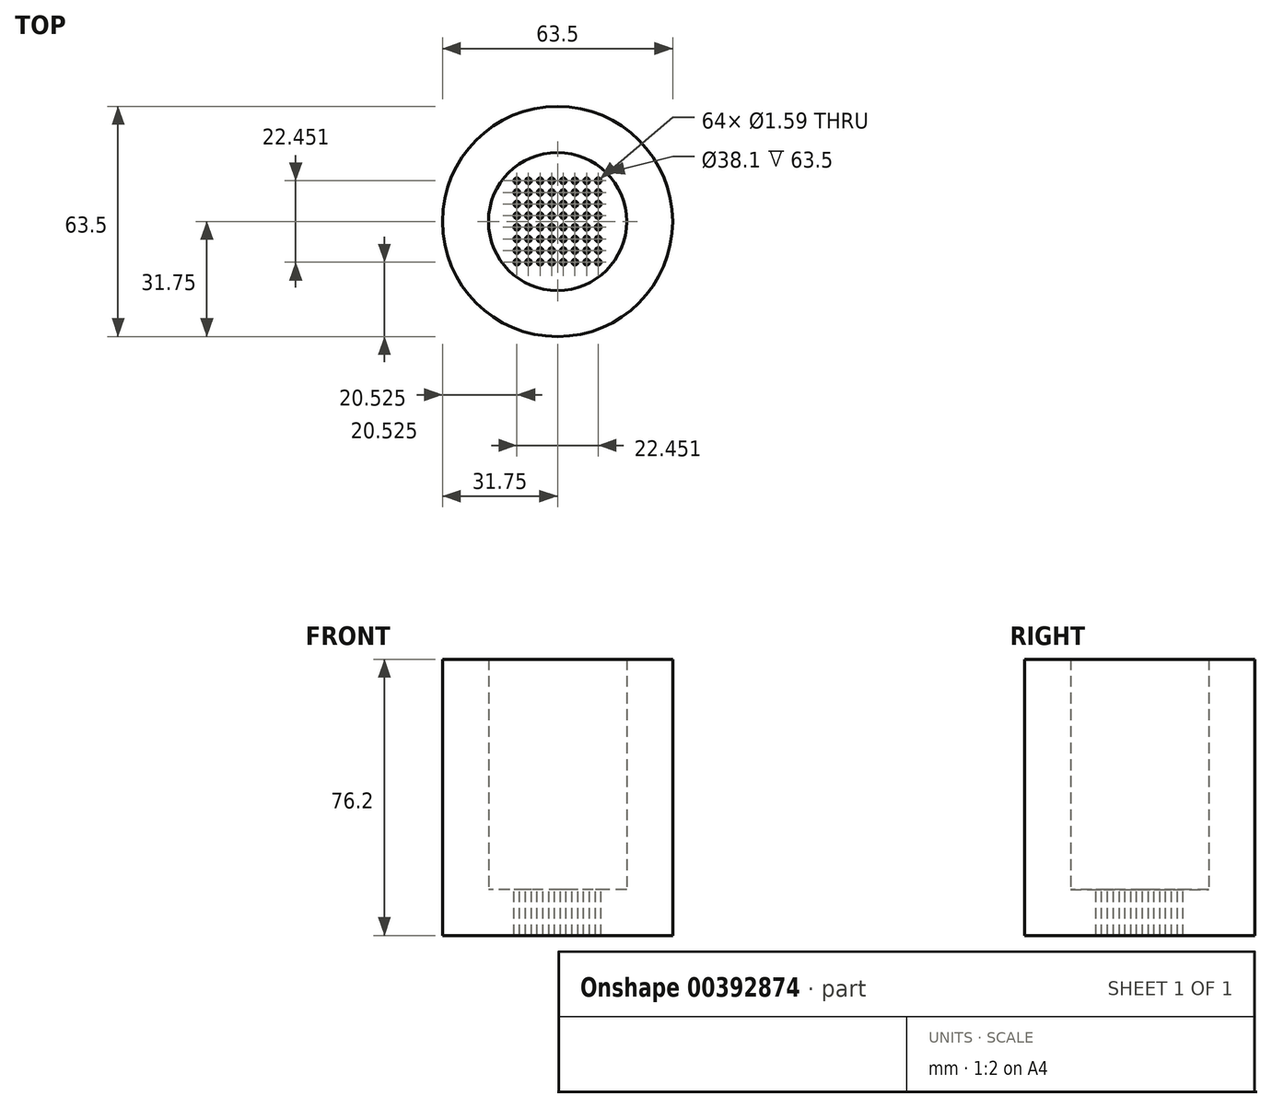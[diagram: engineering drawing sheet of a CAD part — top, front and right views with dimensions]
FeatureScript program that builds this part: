
annotation { "Feature Type Name" : "Feature", "Feature Type Description" : "" }
export const myFeature = defineFeature(function(context is Context, id is Id, definition is map)
    precondition{}
    {
        {
            var Q0;
            Q0=qCreatedBy(makeId("Top.planeOp"),FACE);
            var sketch = newSketch(context, id + "F0", { "sketchPlane" : qUnion([Q0])});
            skCircle(sketch, "E0", {"center": v(0, 0) * mm, "radius": 31.75 * mm});
            skSolve(sketch);
        }
        {
            var Q0;
            Q0=makeQuery(id+"F0.imprint","IMPRINT",FACE,{"disambiguationData":[TD([[makeQuery(id+"F0.imprint","IMPRINT",EDGE,{"derivedFrom":sQuery(id+"F0.wireOp",EDGE,"E0")}),1.0]])]});
            extrude(context, id + "F1", {"entities" : qUnion([Q0]), "depth" : 76.2 * mm});
        }
        {
            var Q0;
            Q0=makeQuery(id+"F1.opExtrude","CAP_FACE",FACE,{"disambiguationData":[OSD([sQuery(id+"F0.wireOp",EDGE,"E0")])],"isStart":false});
            shell(context, id + "F2", {"entities" : qUnion([Q0]), "thickness" : 12.7 * mm});
        }
        {
            var Q0;
            {var subQ0=sQuery(id+"F0.wireOp",EDGE,"E0");Q0=makeQuery(id+"F2.opShell","OFFSET_FACE",FACE,{"disambiguationData":[OSD([subQ0]),TDD([makeQuery(id+"F1.opExtrude","CAP_FACE",FACE,{"disambiguationData":[OSD([subQ0])],"isStart":true})])]});}
            var sketch = newSketch(context, id + "F3", { "sketchPlane" : qUnion([Q0])});
            skCircle(sketch, "E1.0", {"center": v(0, 0) * mm, "radius": 15.87 * mm, "construction": true});
            skLineSegment(sketch, "E2.bottom", {"start": v(-11.23, 11.23) * mm, "end": v(11.23, 11.23) * mm, "construction": true});
            skLineSegment(sketch, "E2.top", {"start": v(-11.23, -11.23) * mm, "end": v(11.23, -11.23) * mm, "construction": true});
            skLineSegment(sketch, "E2.left", {"start": v(-11.23, 11.23) * mm, "end": v(-11.23, -11.23) * mm, "construction": true});
            skLineSegment(sketch, "E2.right", {"start": v(11.23, 11.23) * mm, "end": v(11.23, -11.23) * mm, "construction": true});
            skCircle(sketch, "E3", {"center": v(-11.23, -11.23) * mm, "radius": 0.8 * mm});
            skCircle(sketch, "E4.1.0.0", {"center": v(-8.02, -11.23) * mm, "radius": 0.8 * mm});
            skCircle(sketch, "E4.2.0.0", {"center": v(-4.81, -11.23) * mm, "radius": 0.8 * mm});
            skCircle(sketch, "E4.3.0.0", {"center": v(-1.6, -11.23) * mm, "radius": 0.8 * mm});
            skCircle(sketch, "E4.4.0.0", {"center": v(1.6, -11.23) * mm, "radius": 0.8 * mm});
            skCircle(sketch, "E4.5.0.0", {"center": v(4.81, -11.23) * mm, "radius": 0.8 * mm});
            skCircle(sketch, "E4.6.0.0", {"center": v(8.02, -11.23) * mm, "radius": 0.8 * mm});
            skCircle(sketch, "E4.7.0.0", {"center": v(11.23, -11.23) * mm, "radius": 0.8 * mm});
            skLineSegment(sketch, "E4.direction1", {"start": v(-11.23, -11.23) * mm, "end": v(-8.02, -11.23) * mm, "construction": true});
            skCircle(sketch, "E5.1.0.0", {"center": v(-11.23, -8.02) * mm, "radius": 0.8 * mm});
            skCircle(sketch, "E5.1.0.1", {"center": v(-8.02, -8.02) * mm, "radius": 0.8 * mm});
            skCircle(sketch, "E5.1.0.2", {"center": v(-4.81, -8.02) * mm, "radius": 0.8 * mm});
            skCircle(sketch, "E5.1.0.3", {"center": v(-1.6, -8.02) * mm, "radius": 0.8 * mm});
            skCircle(sketch, "E5.1.0.4", {"center": v(1.6, -8.02) * mm, "radius": 0.8 * mm});
            skCircle(sketch, "E5.1.0.5", {"center": v(4.81, -8.02) * mm, "radius": 0.8 * mm});
            skCircle(sketch, "E5.1.0.6", {"center": v(8.02, -8.02) * mm, "radius": 0.8 * mm});
            skCircle(sketch, "E5.1.0.7", {"center": v(11.23, -8.02) * mm, "radius": 0.8 * mm});
            skCircle(sketch, "E5.2.0.0", {"center": v(-11.23, -4.81) * mm, "radius": 0.8 * mm});
            skCircle(sketch, "E5.2.0.1", {"center": v(-8.02, -4.81) * mm, "radius": 0.8 * mm});
            skCircle(sketch, "E5.2.0.2", {"center": v(-4.81, -4.81) * mm, "radius": 0.8 * mm});
            skCircle(sketch, "E5.2.0.3", {"center": v(-1.6, -4.81) * mm, "radius": 0.8 * mm});
            skCircle(sketch, "E5.2.0.4", {"center": v(1.6, -4.81) * mm, "radius": 0.8 * mm});
            skCircle(sketch, "E5.2.0.5", {"center": v(4.81, -4.81) * mm, "radius": 0.8 * mm});
            skCircle(sketch, "E5.2.0.6", {"center": v(8.02, -4.81) * mm, "radius": 0.8 * mm});
            skCircle(sketch, "E5.2.0.7", {"center": v(11.23, -4.81) * mm, "radius": 0.8 * mm});
            skCircle(sketch, "E5.3.0.0", {"center": v(-11.23, -1.6) * mm, "radius": 0.8 * mm});
            skCircle(sketch, "E5.3.0.1", {"center": v(-8.02, -1.6) * mm, "radius": 0.8 * mm});
            skCircle(sketch, "E5.3.0.2", {"center": v(-4.81, -1.6) * mm, "radius": 0.8 * mm});
            skCircle(sketch, "E5.3.0.3", {"center": v(-1.6, -1.6) * mm, "radius": 0.8 * mm});
            skCircle(sketch, "E5.3.0.4", {"center": v(1.6, -1.6) * mm, "radius": 0.8 * mm});
            skCircle(sketch, "E5.3.0.5", {"center": v(4.81, -1.6) * mm, "radius": 0.8 * mm});
            skCircle(sketch, "E5.3.0.6", {"center": v(8.02, -1.6) * mm, "radius": 0.8 * mm});
            skCircle(sketch, "E5.3.0.7", {"center": v(11.23, -1.6) * mm, "radius": 0.8 * mm});
            skCircle(sketch, "E5.4.0.0", {"center": v(-11.23, 1.6) * mm, "radius": 0.8 * mm});
            skCircle(sketch, "E5.4.0.1", {"center": v(-8.02, 1.6) * mm, "radius": 0.8 * mm});
            skCircle(sketch, "E5.4.0.2", {"center": v(-4.81, 1.6) * mm, "radius": 0.8 * mm});
            skCircle(sketch, "E5.4.0.3", {"center": v(-1.6, 1.6) * mm, "radius": 0.8 * mm});
            skCircle(sketch, "E5.4.0.4", {"center": v(1.6, 1.6) * mm, "radius": 0.8 * mm});
            skCircle(sketch, "E5.4.0.5", {"center": v(4.81, 1.6) * mm, "radius": 0.8 * mm});
            skCircle(sketch, "E5.4.0.6", {"center": v(8.02, 1.6) * mm, "radius": 0.8 * mm});
            skCircle(sketch, "E5.4.0.7", {"center": v(11.23, 1.6) * mm, "radius": 0.8 * mm});
            skCircle(sketch, "E5.5.0.0", {"center": v(-11.23, 4.81) * mm, "radius": 0.8 * mm});
            skCircle(sketch, "E5.5.0.1", {"center": v(-8.02, 4.81) * mm, "radius": 0.8 * mm});
            skCircle(sketch, "E5.5.0.2", {"center": v(-4.81, 4.81) * mm, "radius": 0.8 * mm});
            skCircle(sketch, "E5.5.0.3", {"center": v(-1.6, 4.81) * mm, "radius": 0.8 * mm});
            skCircle(sketch, "E5.5.0.4", {"center": v(1.6, 4.81) * mm, "radius": 0.8 * mm});
            skCircle(sketch, "E5.5.0.5", {"center": v(4.81, 4.81) * mm, "radius": 0.8 * mm});
            skCircle(sketch, "E5.5.0.6", {"center": v(8.02, 4.81) * mm, "radius": 0.8 * mm});
            skCircle(sketch, "E5.5.0.7", {"center": v(11.23, 4.81) * mm, "radius": 0.8 * mm});
            skCircle(sketch, "E5.6.0.0", {"center": v(-11.23, 8.02) * mm, "radius": 0.8 * mm});
            skCircle(sketch, "E5.6.0.1", {"center": v(-8.02, 8.02) * mm, "radius": 0.8 * mm});
            skCircle(sketch, "E5.6.0.2", {"center": v(-4.81, 8.02) * mm, "radius": 0.8 * mm});
            skCircle(sketch, "E5.6.0.3", {"center": v(-1.6, 8.02) * mm, "radius": 0.8 * mm});
            skCircle(sketch, "E5.6.0.4", {"center": v(1.6, 8.02) * mm, "radius": 0.8 * mm});
            skCircle(sketch, "E5.6.0.5", {"center": v(4.81, 8.02) * mm, "radius": 0.8 * mm});
            skCircle(sketch, "E5.6.0.6", {"center": v(8.02, 8.02) * mm, "radius": 0.8 * mm});
            skCircle(sketch, "E5.6.0.7", {"center": v(11.23, 8.02) * mm, "radius": 0.8 * mm});
            skCircle(sketch, "E5.7.0.0", {"center": v(-11.23, 11.23) * mm, "radius": 0.8 * mm});
            skCircle(sketch, "E5.7.0.1", {"center": v(-8.02, 11.23) * mm, "radius": 0.8 * mm});
            skCircle(sketch, "E5.7.0.2", {"center": v(-4.81, 11.23) * mm, "radius": 0.8 * mm});
            skCircle(sketch, "E5.7.0.3", {"center": v(-1.6, 11.23) * mm, "radius": 0.8 * mm});
            skCircle(sketch, "E5.7.0.4", {"center": v(1.6, 11.23) * mm, "radius": 0.8 * mm});
            skCircle(sketch, "E5.7.0.5", {"center": v(4.81, 11.23) * mm, "radius": 0.8 * mm});
            skCircle(sketch, "E5.7.0.6", {"center": v(8.02, 11.23) * mm, "radius": 0.8 * mm});
            skCircle(sketch, "E5.7.0.7", {"center": v(11.23, 11.23) * mm, "radius": 0.8 * mm});
            skLineSegment(sketch, "E5.direction1", {"start": v(-11.23, -11.23) * mm, "end": v(-11.23, -8.02) * mm, "construction": true});
            skSolve(sketch);
        }
        {
            var Q0;
            Q0=makeQuery(id+"F3.imprint","IMPRINT",FACE,{"disambiguationData":[TD([[makeQuery(id+"F3.imprint","IMPRINT",EDGE,{"derivedFrom":sQuery(id+"F3.wireOp",EDGE,"E4.7.0.0")}),1.0]])]});
            var Q1;
            Q1=makeQuery(id+"F3.imprint","IMPRINT",FACE,{"disambiguationData":[TD([[makeQuery(id+"F3.imprint","IMPRINT",EDGE,{"derivedFrom":sQuery(id+"F3.wireOp",EDGE,"E5.1.0.7")}),1.0]])]});
            var Q2;
            Q2=makeQuery(id+"F3.imprint","IMPRINT",FACE,{"disambiguationData":[TD([[makeQuery(id+"F3.imprint","IMPRINT",EDGE,{"derivedFrom":sQuery(id+"F3.wireOp",EDGE,"E5.2.0.7")}),1.0]])]});
            var Q3;
            Q3=makeQuery(id+"F3.imprint","IMPRINT",FACE,{"disambiguationData":[TD([[makeQuery(id+"F3.imprint","IMPRINT",EDGE,{"derivedFrom":sQuery(id+"F3.wireOp",EDGE,"E5.3.0.7")}),1.0]])]});
            var Q4;
            Q4=makeQuery(id+"F3.imprint","IMPRINT",FACE,{"disambiguationData":[TD([[makeQuery(id+"F3.imprint","IMPRINT",EDGE,{"derivedFrom":sQuery(id+"F3.wireOp",EDGE,"E5.4.0.7")}),1.0]])]});
            var Q5;
            Q5=makeQuery(id+"F3.imprint","IMPRINT",FACE,{"disambiguationData":[TD([[makeQuery(id+"F3.imprint","IMPRINT",EDGE,{"derivedFrom":sQuery(id+"F3.wireOp",EDGE,"E5.5.0.7")}),1.0]])]});
            var Q6;
            Q6=makeQuery(id+"F3.imprint","IMPRINT",FACE,{"disambiguationData":[TD([[makeQuery(id+"F3.imprint","IMPRINT",EDGE,{"derivedFrom":sQuery(id+"F3.wireOp",EDGE,"E5.5.0.6")}),1.0]])]});
            var Q7;
            Q7=makeQuery(id+"F3.imprint","IMPRINT",FACE,{"disambiguationData":[TD([[makeQuery(id+"F3.imprint","IMPRINT",EDGE,{"derivedFrom":sQuery(id+"F3.wireOp",EDGE,"E5.6.0.7")}),1.0]])]});
            var Q8;
            Q8=makeQuery(id+"F3.imprint","IMPRINT",FACE,{"disambiguationData":[TD([[makeQuery(id+"F3.imprint","IMPRINT",EDGE,{"derivedFrom":sQuery(id+"F3.wireOp",EDGE,"E5.7.0.7")}),1.0]])]});
            var Q9;
            Q9=makeQuery(id+"F3.imprint","IMPRINT",FACE,{"disambiguationData":[TD([[makeQuery(id+"F3.imprint","IMPRINT",EDGE,{"derivedFrom":sQuery(id+"F3.wireOp",EDGE,"E5.7.0.6")}),1.0]])]});
            var Q10;
            Q10=makeQuery(id+"F3.imprint","IMPRINT",FACE,{"disambiguationData":[TD([[makeQuery(id+"F3.imprint","IMPRINT",EDGE,{"derivedFrom":sQuery(id+"F3.wireOp",EDGE,"E5.6.0.6")}),1.0]])]});
            var Q11;
            Q11=makeQuery(id+"F3.imprint","IMPRINT",FACE,{"disambiguationData":[TD([[makeQuery(id+"F3.imprint","IMPRINT",EDGE,{"derivedFrom":sQuery(id+"F3.wireOp",EDGE,"E5.4.0.6")}),1.0]])]});
            var Q12;
            Q12=makeQuery(id+"F3.imprint","IMPRINT",FACE,{"disambiguationData":[TD([[makeQuery(id+"F3.imprint","IMPRINT",EDGE,{"derivedFrom":sQuery(id+"F3.wireOp",EDGE,"E5.3.0.6")}),1.0]])]});
            var Q13;
            Q13=makeQuery(id+"F3.imprint","IMPRINT",FACE,{"disambiguationData":[TD([[makeQuery(id+"F3.imprint","IMPRINT",EDGE,{"derivedFrom":sQuery(id+"F3.wireOp",EDGE,"E5.2.0.6")}),1.0]])]});
            var Q14;
            Q14=makeQuery(id+"F3.imprint","IMPRINT",FACE,{"disambiguationData":[TD([[makeQuery(id+"F3.imprint","IMPRINT",EDGE,{"derivedFrom":sQuery(id+"F3.wireOp",EDGE,"E4.6.0.0")}),1.0]])]});
            var Q15;
            Q15=makeQuery(id+"F3.imprint","IMPRINT",FACE,{"disambiguationData":[TD([[makeQuery(id+"F3.imprint","IMPRINT",EDGE,{"derivedFrom":sQuery(id+"F3.wireOp",EDGE,"E5.1.0.6")}),1.0]])]});
            var Q16;
            Q16=makeQuery(id+"F3.imprint","IMPRINT",FACE,{"disambiguationData":[TD([[makeQuery(id+"F3.imprint","IMPRINT",EDGE,{"derivedFrom":sQuery(id+"F3.wireOp",EDGE,"E5.1.0.5")}),1.0]])]});
            var Q17;
            Q17=makeQuery(id+"F3.imprint","IMPRINT",FACE,{"disambiguationData":[TD([[makeQuery(id+"F3.imprint","IMPRINT",EDGE,{"derivedFrom":sQuery(id+"F3.wireOp",EDGE,"E4.5.0.0")}),1.0]])]});
            var Q18;
            Q18=makeQuery(id+"F3.imprint","IMPRINT",FACE,{"disambiguationData":[TD([[makeQuery(id+"F3.imprint","IMPRINT",EDGE,{"derivedFrom":sQuery(id+"F3.wireOp",EDGE,"E5.2.0.5")}),1.0]])]});
            var Q19;
            Q19=makeQuery(id+"F3.imprint","IMPRINT",FACE,{"disambiguationData":[TD([[makeQuery(id+"F3.imprint","IMPRINT",EDGE,{"derivedFrom":sQuery(id+"F3.wireOp",EDGE,"E5.3.0.5")}),1.0]])]});
            var Q20;
            Q20=makeQuery(id+"F3.imprint","IMPRINT",FACE,{"disambiguationData":[TD([[makeQuery(id+"F3.imprint","IMPRINT",EDGE,{"derivedFrom":sQuery(id+"F3.wireOp",EDGE,"E5.4.0.5")}),1.0]])]});
            var Q21;
            Q21=makeQuery(id+"F3.imprint","IMPRINT",FACE,{"disambiguationData":[TD([[makeQuery(id+"F3.imprint","IMPRINT",EDGE,{"derivedFrom":sQuery(id+"F3.wireOp",EDGE,"E5.5.0.5")}),1.0]])]});
            var Q22;
            Q22=makeQuery(id+"F3.imprint","IMPRINT",FACE,{"disambiguationData":[TD([[makeQuery(id+"F3.imprint","IMPRINT",EDGE,{"derivedFrom":sQuery(id+"F3.wireOp",EDGE,"E5.6.0.5")}),1.0]])]});
            var Q23;
            Q23=makeQuery(id+"F3.imprint","IMPRINT",FACE,{"disambiguationData":[TD([[makeQuery(id+"F3.imprint","IMPRINT",EDGE,{"derivedFrom":sQuery(id+"F3.wireOp",EDGE,"E5.7.0.5")}),1.0]])]});
            var Q24;
            Q24=makeQuery(id+"F3.imprint","IMPRINT",FACE,{"disambiguationData":[TD([[makeQuery(id+"F3.imprint","IMPRINT",EDGE,{"derivedFrom":sQuery(id+"F3.wireOp",EDGE,"E4.4.0.0")}),1.0]])]});
            var Q25;
            Q25=makeQuery(id+"F3.imprint","IMPRINT",FACE,{"disambiguationData":[TD([[makeQuery(id+"F3.imprint","IMPRINT",EDGE,{"derivedFrom":sQuery(id+"F3.wireOp",EDGE,"E5.2.0.4")}),1.0]])]});
            var Q26;
            Q26=makeQuery(id+"F3.imprint","IMPRINT",FACE,{"disambiguationData":[TD([[makeQuery(id+"F3.imprint","IMPRINT",EDGE,{"derivedFrom":sQuery(id+"F3.wireOp",EDGE,"E5.1.0.4")}),1.0]])]});
            var Q27;
            Q27=makeQuery(id+"F3.imprint","IMPRINT",FACE,{"disambiguationData":[TD([[makeQuery(id+"F3.imprint","IMPRINT",EDGE,{"derivedFrom":sQuery(id+"F3.wireOp",EDGE,"E5.3.0.4")}),1.0]])]});
            var Q28;
            Q28=makeQuery(id+"F3.imprint","IMPRINT",FACE,{"disambiguationData":[TD([[makeQuery(id+"F3.imprint","IMPRINT",EDGE,{"derivedFrom":sQuery(id+"F3.wireOp",EDGE,"E5.4.0.4")}),1.0]])]});
            var Q29;
            Q29=makeQuery(id+"F3.imprint","IMPRINT",FACE,{"disambiguationData":[TD([[makeQuery(id+"F3.imprint","IMPRINT",EDGE,{"derivedFrom":sQuery(id+"F3.wireOp",EDGE,"E5.5.0.4")}),1.0]])]});
            var Q30;
            Q30=makeQuery(id+"F3.imprint","IMPRINT",FACE,{"disambiguationData":[TD([[makeQuery(id+"F3.imprint","IMPRINT",EDGE,{"derivedFrom":sQuery(id+"F3.wireOp",EDGE,"E5.6.0.4")}),1.0]])]});
            var Q31;
            Q31=makeQuery(id+"F3.imprint","IMPRINT",FACE,{"disambiguationData":[TD([[makeQuery(id+"F3.imprint","IMPRINT",EDGE,{"derivedFrom":sQuery(id+"F3.wireOp",EDGE,"E5.7.0.4")}),1.0]])]});
            var Q32;
            Q32=makeQuery(id+"F3.imprint","IMPRINT",FACE,{"disambiguationData":[TD([[makeQuery(id+"F3.imprint","IMPRINT",EDGE,{"derivedFrom":sQuery(id+"F3.wireOp",EDGE,"E5.7.0.3")}),1.0]])]});
            var Q33;
            Q33=makeQuery(id+"F3.imprint","IMPRINT",FACE,{"disambiguationData":[TD([[makeQuery(id+"F3.imprint","IMPRINT",EDGE,{"derivedFrom":sQuery(id+"F3.wireOp",EDGE,"E4.3.0.0")}),1.0]])]});
            var Q34;
            Q34=makeQuery(id+"F3.imprint","IMPRINT",FACE,{"disambiguationData":[TD([[makeQuery(id+"F3.imprint","IMPRINT",EDGE,{"derivedFrom":sQuery(id+"F3.wireOp",EDGE,"E4.2.0.0")}),1.0]])]});
            var Q35;
            Q35=makeQuery(id+"F3.imprint","IMPRINT",FACE,{"disambiguationData":[TD([[makeQuery(id+"F3.imprint","IMPRINT",EDGE,{"derivedFrom":sQuery(id+"F3.wireOp",EDGE,"E5.1.0.2")}),1.0]])]});
            var Q36;
            Q36=makeQuery(id+"F3.imprint","IMPRINT",FACE,{"disambiguationData":[TD([[makeQuery(id+"F3.imprint","IMPRINT",EDGE,{"derivedFrom":sQuery(id+"F3.wireOp",EDGE,"E5.1.0.3")}),1.0]])]});
            var Q37;
            Q37=makeQuery(id+"F3.imprint","IMPRINT",FACE,{"disambiguationData":[TD([[makeQuery(id+"F3.imprint","IMPRINT",EDGE,{"derivedFrom":sQuery(id+"F3.wireOp",EDGE,"E5.2.0.3")}),1.0]])]});
            var Q38;
            Q38=makeQuery(id+"F3.imprint","IMPRINT",FACE,{"disambiguationData":[TD([[makeQuery(id+"F3.imprint","IMPRINT",EDGE,{"derivedFrom":sQuery(id+"F3.wireOp",EDGE,"E5.2.0.2")}),1.0]])]});
            var Q39;
            Q39=makeQuery(id+"F3.imprint","IMPRINT",FACE,{"disambiguationData":[TD([[makeQuery(id+"F3.imprint","IMPRINT",EDGE,{"derivedFrom":sQuery(id+"F3.wireOp",EDGE,"E5.3.0.2")}),1.0]])]});
            var Q40;
            Q40=makeQuery(id+"F3.imprint","IMPRINT",FACE,{"disambiguationData":[TD([[makeQuery(id+"F3.imprint","IMPRINT",EDGE,{"derivedFrom":sQuery(id+"F3.wireOp",EDGE,"E5.3.0.3")}),1.0]])]});
            var Q41;
            Q41=makeQuery(id+"F3.imprint","IMPRINT",FACE,{"disambiguationData":[TD([[makeQuery(id+"F3.imprint","IMPRINT",EDGE,{"derivedFrom":sQuery(id+"F3.wireOp",EDGE,"E5.4.0.3")}),1.0]])]});
            var Q42;
            Q42=makeQuery(id+"F3.imprint","IMPRINT",FACE,{"disambiguationData":[TD([[makeQuery(id+"F3.imprint","IMPRINT",EDGE,{"derivedFrom":sQuery(id+"F3.wireOp",EDGE,"E5.4.0.2")}),1.0]])]});
            var Q43;
            Q43=makeQuery(id+"F3.imprint","IMPRINT",FACE,{"disambiguationData":[TD([[makeQuery(id+"F3.imprint","IMPRINT",EDGE,{"derivedFrom":sQuery(id+"F3.wireOp",EDGE,"E5.5.0.2")}),1.0]])]});
            var Q44;
            Q44=makeQuery(id+"F3.imprint","IMPRINT",FACE,{"disambiguationData":[TD([[makeQuery(id+"F3.imprint","IMPRINT",EDGE,{"derivedFrom":sQuery(id+"F3.wireOp",EDGE,"E5.5.0.3")}),1.0]])]});
            var Q45;
            Q45=makeQuery(id+"F3.imprint","IMPRINT",FACE,{"disambiguationData":[TD([[makeQuery(id+"F3.imprint","IMPRINT",EDGE,{"derivedFrom":sQuery(id+"F3.wireOp",EDGE,"E5.6.0.3")}),1.0]])]});
            var Q46;
            Q46=makeQuery(id+"F3.imprint","IMPRINT",FACE,{"disambiguationData":[TD([[makeQuery(id+"F3.imprint","IMPRINT",EDGE,{"derivedFrom":sQuery(id+"F3.wireOp",EDGE,"E5.6.0.2")}),1.0]])]});
            var Q47;
            Q47=makeQuery(id+"F3.imprint","IMPRINT",FACE,{"disambiguationData":[TD([[makeQuery(id+"F3.imprint","IMPRINT",EDGE,{"derivedFrom":sQuery(id+"F3.wireOp",EDGE,"E5.7.0.2")}),1.0]])]});
            var Q48;
            Q48=makeQuery(id+"F3.imprint","IMPRINT",FACE,{"disambiguationData":[TD([[makeQuery(id+"F3.imprint","IMPRINT",EDGE,{"derivedFrom":sQuery(id+"F3.wireOp",EDGE,"E5.6.0.1")}),1.0]])]});
            var Q49;
            Q49=makeQuery(id+"F3.imprint","IMPRINT",FACE,{"disambiguationData":[TD([[makeQuery(id+"F3.imprint","IMPRINT",EDGE,{"derivedFrom":sQuery(id+"F3.wireOp",EDGE,"E5.7.0.1")}),1.0]])]});
            var Q50;
            Q50=makeQuery(id+"F3.imprint","IMPRINT",FACE,{"disambiguationData":[TD([[makeQuery(id+"F3.imprint","IMPRINT",EDGE,{"derivedFrom":sQuery(id+"F3.wireOp",EDGE,"E5.7.0.0")}),1.0]])]});
            var Q51;
            Q51=makeQuery(id+"F3.imprint","IMPRINT",FACE,{"disambiguationData":[TD([[makeQuery(id+"F3.imprint","IMPRINT",EDGE,{"derivedFrom":sQuery(id+"F3.wireOp",EDGE,"E5.6.0.0")}),1.0]])]});
            var Q52;
            Q52=makeQuery(id+"F3.imprint","IMPRINT",FACE,{"disambiguationData":[TD([[makeQuery(id+"F3.imprint","IMPRINT",EDGE,{"derivedFrom":sQuery(id+"F3.wireOp",EDGE,"E5.5.0.0")}),1.0]])]});
            var Q53;
            Q53=makeQuery(id+"F3.imprint","IMPRINT",FACE,{"disambiguationData":[TD([[makeQuery(id+"F3.imprint","IMPRINT",EDGE,{"derivedFrom":sQuery(id+"F3.wireOp",EDGE,"E5.5.0.1")}),1.0]])]});
            var Q54;
            Q54=makeQuery(id+"F3.imprint","IMPRINT",FACE,{"disambiguationData":[TD([[makeQuery(id+"F3.imprint","IMPRINT",EDGE,{"derivedFrom":sQuery(id+"F3.wireOp",EDGE,"E5.4.0.0")}),1.0]])]});
            var Q55;
            Q55=makeQuery(id+"F3.imprint","IMPRINT",FACE,{"disambiguationData":[TD([[makeQuery(id+"F3.imprint","IMPRINT",EDGE,{"derivedFrom":sQuery(id+"F3.wireOp",EDGE,"E5.4.0.1")}),1.0]])]});
            var Q56;
            Q56=makeQuery(id+"F3.imprint","IMPRINT",FACE,{"disambiguationData":[TD([[makeQuery(id+"F3.imprint","IMPRINT",EDGE,{"derivedFrom":sQuery(id+"F3.wireOp",EDGE,"E5.3.0.1")}),1.0]])]});
            var Q57;
            Q57=makeQuery(id+"F3.imprint","IMPRINT",FACE,{"disambiguationData":[TD([[makeQuery(id+"F3.imprint","IMPRINT",EDGE,{"derivedFrom":sQuery(id+"F3.wireOp",EDGE,"E5.3.0.0")}),1.0]])]});
            var Q58;
            Q58=makeQuery(id+"F3.imprint","IMPRINT",FACE,{"disambiguationData":[TD([[makeQuery(id+"F3.imprint","IMPRINT",EDGE,{"derivedFrom":sQuery(id+"F3.wireOp",EDGE,"E5.2.0.0")}),1.0]])]});
            var Q59;
            Q59=makeQuery(id+"F3.imprint","IMPRINT",FACE,{"disambiguationData":[TD([[makeQuery(id+"F3.imprint","IMPRINT",EDGE,{"derivedFrom":sQuery(id+"F3.wireOp",EDGE,"E5.2.0.1")}),1.0]])]});
            var Q60;
            Q60=makeQuery(id+"F3.imprint","IMPRINT",FACE,{"disambiguationData":[TD([[makeQuery(id+"F3.imprint","IMPRINT",EDGE,{"derivedFrom":sQuery(id+"F3.wireOp",EDGE,"E5.1.0.1")}),1.0]])]});
            var Q61;
            Q61=makeQuery(id+"F3.imprint","IMPRINT",FACE,{"disambiguationData":[TD([[makeQuery(id+"F3.imprint","IMPRINT",EDGE,{"derivedFrom":sQuery(id+"F3.wireOp",EDGE,"E5.1.0.0")}),1.0]])]});
            var Q62;
            Q62=makeQuery(id+"F3.imprint","IMPRINT",FACE,{"disambiguationData":[TD([[makeQuery(id+"F3.imprint","IMPRINT",EDGE,{"derivedFrom":sQuery(id+"F3.wireOp",EDGE,"E3")}),1.0]])]});
            var Q63;
            Q63=makeQuery(id+"F3.imprint","IMPRINT",FACE,{"disambiguationData":[TD([[makeQuery(id+"F3.imprint","IMPRINT",EDGE,{"derivedFrom":sQuery(id+"F3.wireOp",EDGE,"E4.1.0.0")}),1.0]])]});
            var Q64;
            Q64=makeQuery(id+"F1.opExtrude","CAP_FACE",FACE,{"disambiguationData":[OSD([sQuery(id+"F0.wireOp",EDGE,"E0")])],"isStart":true});
            extrude(context, id + "F4", {"entities" : qUnion([Q0, Q1, Q2, Q3, Q4, Q5, Q6, Q7, Q8, Q9, Q10, Q11, Q12, Q13, Q14, Q15, Q16, Q17, Q18, Q19, Q20, Q21, Q22, Q23, Q24, Q25, Q26, Q27, Q28, Q29, Q30, Q31, Q32, Q33, Q34, Q35, Q36, Q37, Q38, Q39, Q40, Q41, Q42, Q43, Q44, Q45, Q46, Q47, Q48, Q49, Q50, Q51, Q52, Q53, Q54, Q55, Q56, Q57, Q58, Q59, Q60, Q61, Q62, Q63]), "operationType" : NewBodyOperationType.REMOVE, "endBound" : BoundingType.UP_TO_SURFACE, "oppositeDirection" : true, "endBoundEntityFace" : qUnion([Q64]), "depth" : 25.4 * mm});
        }
    });
